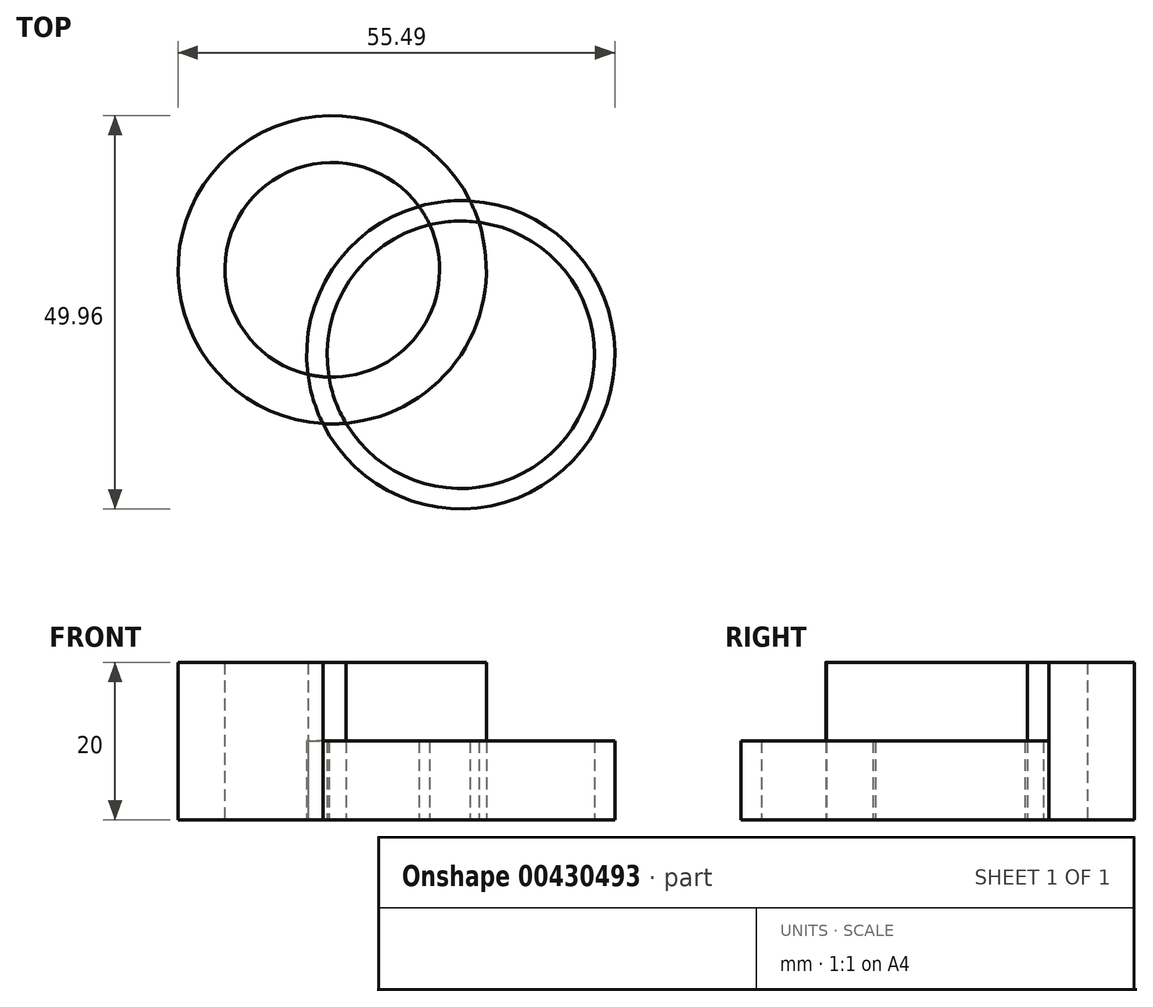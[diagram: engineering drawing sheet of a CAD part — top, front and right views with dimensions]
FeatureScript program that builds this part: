
annotation { "Feature Type Name" : "Feature", "Feature Type Description" : "" }
export const myFeature = defineFeature(function(context is Context, id is Id, definition is map)
    precondition{}
    {
        {
            var Q0;
            Q0=qCreatedBy(makeId("Top.planeOp"),FACE);
            var sketch = newSketch(context, id + "F0", { "sketchPlane" : qUnion([Q0])});
            skCircle(sketch, "E0", {"center": v(0, 0) * mm, "radius": 19.58 * mm});
            skCircle(sketch, "E1", {"center": v(16.33, -10.8) * mm, "radius": 19.58 * mm});
            skCircle(sketch, "E2", {"center": v(0, 0) * mm, "radius": 13.64 * mm});
            skCircle(sketch, "E3", {"center": v(16.33, -10.8) * mm, "radius": 16.99 * mm});
            skSolve(sketch);
        }
        {
            var Q0;
            {var subQ0=sQuery(id+"F0.wireOp",EDGE,"E1");var subQ1=sQuery(id+"F0.wireOp",EDGE,"E0");var subQ2=makeQuery(id+"F0.imprint","INTERSECT",VERTEX,{"disambiguationData":[OD(0.0)],"derivedFrom":[subQ1,subQ0]});Q0=makeQuery(id+"F0.imprint","IMPRINT",FACE,{"disambiguationData":[TD([[makeQuery(id+"F0.imprint","IMPRINT",EDGE,{"disambiguationData":[TD([[subQ2,-1.0]])],"derivedFrom":subQ1}),1.0]])]});}
            extrude(context, id + "F1", {"entities" : qUnion([Q0]), "depth" : 20 * mm});
        }
        {
            var Q0;
            {var subQ0=sQuery(id+"F0.wireOp",EDGE,"E3");var subQ1=sQuery(id+"F0.wireOp",EDGE,"E0");var subQ2=makeQuery(id+"F0.imprint","INTERSECT",VERTEX,{"disambiguationData":[OD(0.0)],"derivedFrom":[subQ1,subQ0]});Q0=makeQuery(id+"F0.imprint","IMPRINT",FACE,{"disambiguationData":[TD([[makeQuery(id+"F0.imprint","IMPRINT",EDGE,{"disambiguationData":[TD([[subQ2,1.0]])],"derivedFrom":subQ1}),1.0]])]});}
            extrude(context, id + "F2", {"entities" : qUnion([Q0]), "depth" : 20 * mm});
        }
        {
            var Q0;
            {var subQ0=sQuery(id+"F0.wireOp",EDGE,"E1");var subQ1=sQuery(id+"F0.wireOp",EDGE,"E0");var subQ2=makeQuery(id+"F0.imprint","INTERSECT",VERTEX,{"disambiguationData":[OD(1.0)],"derivedFrom":[subQ1,subQ0]});Q0=makeQuery(id+"F0.imprint","IMPRINT",FACE,{"disambiguationData":[TD([[makeQuery(id+"F0.imprint","IMPRINT",EDGE,{"disambiguationData":[TD([[subQ2,-1.0]])],"derivedFrom":subQ1}),1.0]])]});}
            extrude(context, id + "F3", {"entities" : qUnion([Q0]), "depth" : 20 * mm});
        }
        {
            var Q0;
            {var subQ0=sQuery(id+"F0.wireOp",EDGE,"E1");var subQ1=sQuery(id+"F0.wireOp",EDGE,"E0");var subQ2=makeQuery(id+"F0.imprint","INTERSECT",VERTEX,{"disambiguationData":[OD(0.0)],"derivedFrom":[subQ1,subQ0]});Q0=makeQuery(id+"F0.imprint","IMPRINT",FACE,{"disambiguationData":[TD([[makeQuery(id+"F0.imprint","IMPRINT",EDGE,{"disambiguationData":[TD([[subQ2,1.0]])],"derivedFrom":subQ1}),1.0]])]});}
            extrude(context, id + "F4", {"entities" : qUnion([Q0]), "depth" : 20 * mm});
        }
        {
            var Q0;
            {var subQ0=sQuery(id+"F0.wireOp",EDGE,"E1");var subQ1=sQuery(id+"F0.wireOp",EDGE,"E0");var subQ2=makeQuery(id+"F0.imprint","INTERSECT",VERTEX,{"disambiguationData":[OD(0.0)],"derivedFrom":[subQ1,subQ0]});Q0=makeQuery(id+"F0.imprint","IMPRINT",FACE,{"disambiguationData":[TD([[makeQuery(id+"F0.imprint","IMPRINT",EDGE,{"disambiguationData":[TD([[subQ2,1.0]])],"derivedFrom":subQ1}),-1.0]])]});}
            extrude(context, id + "F5", {"entities" : qUnion([Q0]), "depth" : 10 * mm});
        }
        {
            var Q0;
            {var subQ0=sQuery(id+"F0.wireOp",EDGE,"E2");var subQ1=sQuery(id+"F0.wireOp",EDGE,"E1");var subQ2=makeQuery(id+"F0.imprint","INTERSECT",VERTEX,{"disambiguationData":[OD(0.0)],"derivedFrom":[subQ1,subQ0]});Q0=makeQuery(id+"F0.imprint","IMPRINT",FACE,{"disambiguationData":[TD([[makeQuery(id+"F0.imprint","IMPRINT",EDGE,{"disambiguationData":[TD([[subQ2,-1.0]])],"derivedFrom":subQ1}),1.0]])]});}
            extrude(context, id + "F6", {"entities" : qUnion([Q0]), "depth" : 10 * mm});
        }
    });
